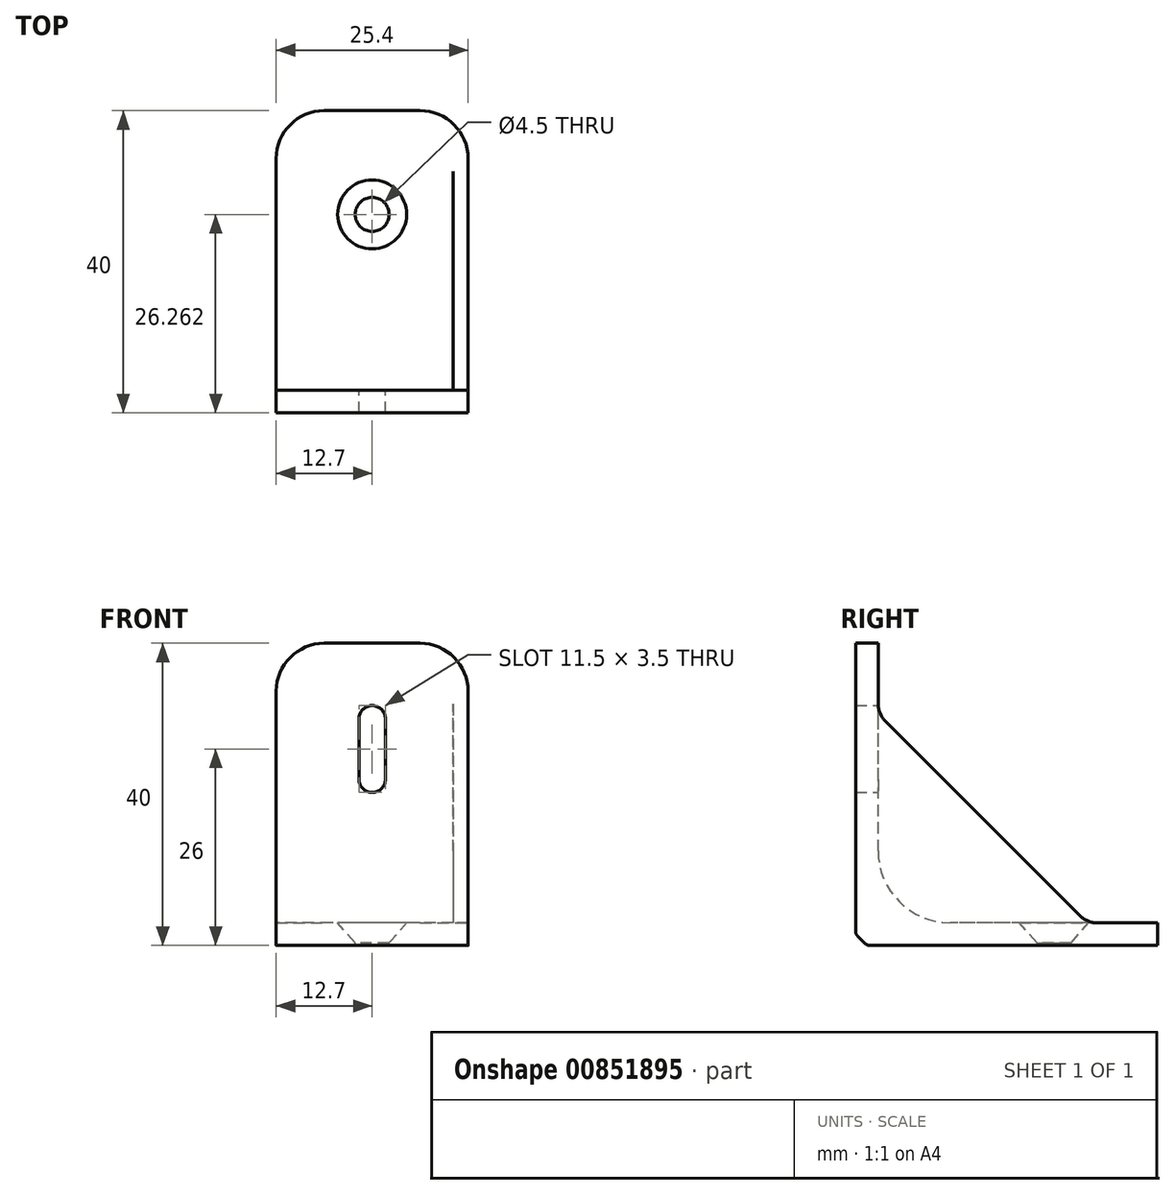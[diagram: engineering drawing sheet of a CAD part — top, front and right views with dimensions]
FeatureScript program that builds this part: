
annotation { "Feature Type Name" : "Feature", "Feature Type Description" : "" }
export const myFeature = defineFeature(function(context is Context, id is Id, definition is map)
    precondition{}
    {
        {
            var Q0;
            Q0=qCreatedBy(makeId("Right.planeOp"),FACE);
            var sketch = newSketch(context, id + "F0", { "sketchPlane" : qUnion([Q0])});
            skLineSegment(sketch, "E0", {"start": v(0, 40) * mm, "end": v(0, 0) * mm});
            skLineSegment(sketch, "E1", {"start": v(0, 0) * mm, "end": v(40, 0) * mm});
            skLineSegment(sketch, "E2", {"start": v(40, 0) * mm, "end": v(40, 3) * mm});
            skLineSegment(sketch, "E3", {"start": v(40, 3) * mm, "end": v(3, 3) * mm});
            skLineSegment(sketch, "E4", {"start": v(3, 3) * mm, "end": v(3, 40) * mm});
            skLineSegment(sketch, "E5", {"start": v(3, 40) * mm, "end": v(0, 40) * mm});
            skSolve(sketch);
        }
        {
            var Q0;
            Q0 = qSketchRegion(id + "F0", true);
            extrude(context, id + "F1", {"entities" : qUnion([Q0]), "endBound" : BoundingType.SYMMETRIC, "depth" : 25.4 * mm, "offsetDistance" : 25.4 * mm});
        }
        {
            var Q0;
            Q0=makeQuery(id+"F1.opExtrude","SWEPT_EDGE",EDGE,{"disambiguationData":[OSD([sQuery(id+"F0.wireOp",EDGE,"E3"),sQuery(id+"F0.wireOp",EDGE,"E4")])]});
            fillet(context, id + "F2", {"entities" : qUnion([Q0]), "radius" : 9.52 * mm, "tangentPropagation" : true, "allowEdgeOverflow" : false});
        }
        {
            var Q0;
            Q0=makeQuery(id+"F1.opExtrude","SWEPT_EDGE",EDGE,{"disambiguationData":[OSD([sQuery(id+"F0.wireOp",EDGE,"E0"),sQuery(id+"F0.wireOp",EDGE,"E1")])]});
            chamfer(context, id + "F3", {"entities" : qUnion([Q0]), "width" : 1.52 * mm, "tangentPropagation" : true});
        }
        {
            var Q0;
            {var subQ0=sQuery(id+"F0.wireOp",EDGE,"E0");Q0=makeQuery(id+"F3.opChamfer","BLEND_EDGE",EDGE,{"blendedFrom":[makeQuery(id+"F1.opExtrude","SWEPT_EDGE",EDGE,{"disambiguationData":[OSD([subQ0,sQuery(id+"F0.wireOp",EDGE,"E1")])]}),makeQuery(id+"F1.opExtrude","SWEPT_FACE",FACE,{"disambiguationData":[OSD([subQ0])]})],"blendedInto":[makeQuery(id+"F1.opExtrude","SWEPT_FACE",FACE,{"disambiguationData":[OSD([subQ0])]})]});}
            var Q1;
            {var subQ0=sQuery(id+"F0.wireOp",EDGE,"E1");Q1=makeQuery(id+"F3.opChamfer","BLEND_EDGE",EDGE,{"blendedFrom":[makeQuery(id+"F1.opExtrude","SWEPT_EDGE",EDGE,{"disambiguationData":[OSD([sQuery(id+"F0.wireOp",EDGE,"E0"),subQ0])]}),makeQuery(id+"F1.opExtrude","SWEPT_FACE",FACE,{"disambiguationData":[OSD([subQ0])]})],"blendedInto":[makeQuery(id+"F1.opExtrude","SWEPT_FACE",FACE,{"disambiguationData":[OSD([subQ0])]})]});}
            fillet(context, id + "F4", {"entities" : qUnion([Q0, Q1]), "radius" : 1.02 * mm, "tangentPropagation" : true, "allowEdgeOverflow" : false});
        }
        {
            var Q0;
            Q0=makeQuery(id+"F1.opExtrude","CAP_FACE",FACE,{"disambiguationData":[OSD([sQuery(id+"F0.wireOp",EDGE,"E0"),sQuery(id+"F0.wireOp",EDGE,"E1"),sQuery(id+"F0.wireOp",EDGE,"E2"),sQuery(id+"F0.wireOp",EDGE,"E3"),sQuery(id+"F0.wireOp",EDGE,"E4"),sQuery(id+"F0.wireOp",EDGE,"E5")])],"isStart":false});
            var sketch = newSketch(context, id + "F5", { "sketchPlane" : qUnion([Q0])});
            skLineSegment(sketch, "E6.0", {"start": v(0, 40) * mm, "end": v(0, 1.94) * mm});
            skLineSegment(sketch, "E6.1", {"start": v(1.94, 0) * mm, "end": v(40, 0) * mm});
            skArc(sketch, "E6.2", {"start": v(1.23, 0.3) * mm, "mid": v(1.56, 0.08) * mm, "end": v(1.94, 0) * mm});
            skLineSegment(sketch, "E6.3", {"start": v(0.3, 1.23) * mm, "end": v(1.23, 0.3) * mm});
            skArc(sketch, "E6.4", {"start": v(0, 1.94) * mm, "mid": v(0.08, 1.56) * mm, "end": v(0.3, 1.23) * mm});
            skLineSegment(sketch, "E7", {"start": v(0, 33.65) * mm, "end": v(33.65, 0) * mm});
            skSolve(sketch);
        }
        {
            var Q0;
            Q0 = qSketchRegion(id + "F5", true);
            extrude(context, id + "F6", {"entities" : qUnion([Q0]), "operationType" : NewBodyOperationType.ADD, "oppositeDirection" : true, "depth" : 2 * mm, "offsetDistance" : 25.4 * mm});
        }
        {
            var Q0;
            Q0=makeQuery(id+"F1.opExtrude","CAP_EDGE",EDGE,{"disambiguationData":[OSD([sQuery(id+"F0.wireOp",EDGE,"E5")])],"isStart":false});
            var Q1;
            Q1=makeQuery(id+"F1.opExtrude","CAP_EDGE",EDGE,{"disambiguationData":[OSD([sQuery(id+"F0.wireOp",EDGE,"E5")])],"isStart":true});
            var Q2;
            Q2=makeQuery(id+"F1.opExtrude","CAP_EDGE",EDGE,{"disambiguationData":[OSD([sQuery(id+"F0.wireOp",EDGE,"E2")])],"isStart":true});
            var Q3;
            Q3=makeQuery(id+"F1.opExtrude","CAP_EDGE",EDGE,{"disambiguationData":[OSD([sQuery(id+"F0.wireOp",EDGE,"E2")])],"isStart":false});
            fillet(context, id + "F7", {"entities" : qUnion([Q0, Q1, Q2, Q3]), "radius" : 6.35 * mm, "tangentPropagation" : true, "allowEdgeOverflow" : false});
        }
        {
            var Q0;
            Q0=makeQuery(id+"F6.boolean.opBoolean","INTERSECT",EDGE,{"derivedFrom":[makeQuery(id+"F1.opExtrude","SWEPT_FACE",FACE,{"disambiguationData":[OSD([sQuery(id+"F0.wireOp",EDGE,"E4")])]}),makeQuery(id+"F6.opExtrude","SWEPT_FACE",FACE,{"disambiguationData":[OSD([sQuery(id+"F5.wireOp",EDGE,"E7")])]})]});
            var Q1;
            Q1=makeQuery(id+"F41RkwAB5lTpXg3_1.1.F6.boolean.opBoolean","INTERSECT",EDGE,{"derivedFrom":[makeQuery(id+"F1.opExtrude","SWEPT_FACE",FACE,{"disambiguationData":[OSD([sQuery(id+"F0.wireOp",EDGE,"E4")])]}),makeQuery(id+"F41RkwAB5lTpXg3_1.1.F6.opExtrude","SWEPT_FACE",FACE,{"disambiguationData":[OSD([sQuery(id+"F5.wireOp",EDGE,"E7")])]})]});
            var Q2;
            Q2=makeQuery(id+"F41RkwAB5lTpXg3_1.1.F6.boolean.opBoolean","INTERSECT",EDGE,{"derivedFrom":[makeQuery(id+"F1.opExtrude","SWEPT_FACE",FACE,{"disambiguationData":[OSD([sQuery(id+"F0.wireOp",EDGE,"E3")])]}),makeQuery(id+"F41RkwAB5lTpXg3_1.1.F6.opExtrude","SWEPT_FACE",FACE,{"disambiguationData":[OSD([sQuery(id+"F5.wireOp",EDGE,"E7")])]})]});
            var Q3;
            Q3=makeQuery(id+"F6.boolean.opBoolean","INTERSECT",EDGE,{"derivedFrom":[makeQuery(id+"F1.opExtrude","SWEPT_FACE",FACE,{"disambiguationData":[OSD([sQuery(id+"F0.wireOp",EDGE,"E3")])]}),makeQuery(id+"F6.opExtrude","SWEPT_FACE",FACE,{"disambiguationData":[OSD([sQuery(id+"F5.wireOp",EDGE,"E7")])]})]});
            fillet(context, id + "F8", {"entities" : qUnion([Q0, Q1, Q2, Q3]), "radius" : 3.17 * mm, "tangentPropagation" : true, "allowEdgeOverflow" : false});
        }
        {
            var Q0;
            Q0=makeQuery(id+"F1.opExtrude","SWEPT_FACE",FACE,{"disambiguationData":[OSD([sQuery(id+"F0.wireOp",EDGE,"E4")])]});
            var sketch = newSketch(context, id + "F9", { "sketchPlane" : qUnion([Q0])});
            skCircle(sketch, "E8", {"center": v(0, 30) * mm, "radius": 1.75 * mm});
            skCircle(sketch, "E9", {"center": v(0, 22) * mm, "radius": 1.75 * mm});
            skLineSegment(sketch, "E10", {"start": v(-1.75, 30) * mm, "end": v(-1.75, 22) * mm});
            skLineSegment(sketch, "E11", {"start": v(1.75, 22) * mm, "end": v(1.75, 30) * mm});
            skSolve(sketch);
        }
        {
            var Q0;
            {var subQ0=sQuery(id+"F9.wireOp",EDGE,"E10");Q0=makeQuery(id+"F9.imprint","IMPRINT",FACE,{"disambiguationData":[TD([[makeQuery(id+"F9.imprint","IMPRINT",EDGE,{"derivedFrom":subQ0}),1.0]])]});}
            var Q1;
            {var subQ0=sQuery(id+"F9.wireOp",EDGE,"E8");var subQ1=makeQuery(id+"F9.imprint","INTERSECT",VERTEX,{"derivedFrom":[subQ0,sQuery(id+"F9.wireOp",EDGE,"E10")]});Q1=makeQuery(id+"F9.imprint","IMPRINT",FACE,{"disambiguationData":[TD([[makeQuery(id+"F9.imprint","IMPRINT",EDGE,{"disambiguationData":[TD([[subQ1,-1.0]])],"derivedFrom":subQ0}),1.0]])]});}
            var Q2;
            {var subQ0=sQuery(id+"F9.wireOp",EDGE,"E9");var subQ1=makeQuery(id+"F9.imprint","INTERSECT",VERTEX,{"derivedFrom":[subQ0,sQuery(id+"F9.wireOp",EDGE,"E10")]});Q2=makeQuery(id+"F9.imprint","IMPRINT",FACE,{"disambiguationData":[TD([[makeQuery(id+"F9.imprint","IMPRINT",EDGE,{"disambiguationData":[TD([[subQ1,-1.0]])],"derivedFrom":subQ0}),1.0]])]});}
            extrude(context, id + "F10", {"entities" : qUnion([Q0, Q1, Q2]), "operationType" : NewBodyOperationType.REMOVE, "endBound" : BoundingType.THROUGH_ALL, "oppositeDirection" : true, "depth" : 25.4 * mm, "offsetDistance" : 25.4 * mm});
        }
        {
            var Q0;
            Q0=makeQuery(id+"F1.opExtrude","SWEPT_FACE",FACE,{"disambiguationData":[OSD([sQuery(id+"F0.wireOp",EDGE,"E3")])]});
            var sketch = newSketch(context, id + "F11", { "sketchPlane" : qUnion([Q0])});
            skPoint(sketch, "E12", {"position": v(0, 26.26) * mm});
            skLineSegment(sketch, "E13", {"start": v(0, 12.53) * mm, "end": v(0, 40) * mm, "construction": true});
            skSolve(sketch);
        }
        {
            var Q0;
            Q0=sQuery(id+"F11.wireOp",VERTEX,"E12");
            var Q1;
            Q1=makeQuery(id+"F1.opExtrude","SWEPT_BODY",BODY,{"disambiguationData":[OSD([sQuery(id+"F0.wireOp",EDGE,"E0"),sQuery(id+"F0.wireOp",EDGE,"E1"),sQuery(id+"F0.wireOp",EDGE,"E2"),sQuery(id+"F0.wireOp",EDGE,"E3"),sQuery(id+"F0.wireOp",EDGE,"E4"),sQuery(id+"F0.wireOp",EDGE,"E5")])]});
            hole(context, id + "F12", {"style" : HoleStyle.C_SINK, "endStyle" : HoleEndStyle.BLIND, "standardTappedOrClearance" : lookupTablePath({ "fit" : "Normal (ASME)", "standard" : "ANSI", "size" : "#8", "type" : "Clearance" }), "standardBlindInLast" : lookupTablePath({ "fit" : "Free", "standard" : "ANSI", "size" : "#8", "type" : "Clearance" }), "holeDiameter" : 4.5 * mm, "cSinkDiameter" : 9.12 * mm, "cSinkAngle" : 82 * degree, "majorDiameter" : 6.35 * mm, "holeDepth" : 25.4 * mm, "isTappedThrough" : true, "tappedDepth" : 4.06 * mm, "tapClearance" : 3, "locations" : qUnion([Q0]), "scope" : qUnion([Q1])});
        }
    });
